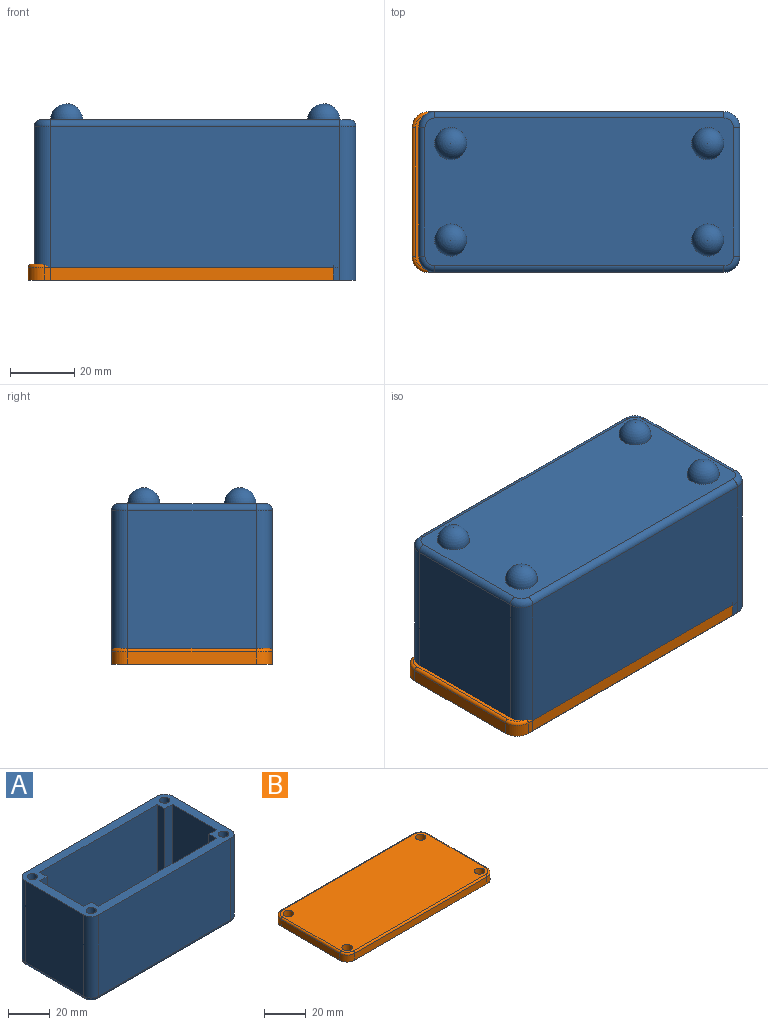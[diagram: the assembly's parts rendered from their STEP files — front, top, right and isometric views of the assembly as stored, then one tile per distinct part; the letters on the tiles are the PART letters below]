
ASSEMBLY  parts=2 mates=1
PART A: 43 faces, bbox 100.8x50.8x55 mm
  f0: plane 90x40mm, normal (0,0,1), area 3500mm2, adj f1,f2,f3,f4,f11,f12,f13,f14
  f1: plane 45x30mm, normal (-1,0,0), area 1350mm2, adj f0,f5,f16,f18
  f2: plane 45x30mm, normal (1,0,0), area 1350mm2, adj f0,f5,f12,f14
  f3: plane 80x45mm, normal (0,1,0), area 3600mm2, adj f0,f5,f13,f17
  f4: plane 80x45mm, normal (0,-1,0), area 3600mm2, adj f0,f5,f11,f15
  f5: plane 100x50mm, normal (0,0,1), area 1400mm2, adj f1,f2,f3,f4,f6,f7,f8,f9
  f6: plane 90x48mm, normal (0,1,0), area 4320mm2, adj f5,f27,f30,f39
  f7: plane 48x40mm, normal (-1,0,0), area 1920mm2, adj f5,f27,f28,f35
  f8: plane 90x48mm, normal (0,-1,0), area 4320mm2, adj f5,f28,f29,f38
  f9: plane 48x40mm, normal (1,0,0), area 1920mm2, adj f5,f29,f30,f42
  f10: plane 96x46mm, normal (0,0,-1), area 4094.1mm2, adj f31,f32,f33,f34,f35,f36,f37,f38
  f11: plane 45x5mm, normal (1,0,0), area 225mm2, adj f0,f4,f5,f12
  f12: plane 45x5mm, normal (0,-1,0), area 225mm2, adj f0,f2,f5,f11
  f13: plane 45x5mm, normal (1,0,0), area 225mm2, adj f0,f3,f5,f14
  f14: plane 45x5mm, normal (0,1,0), area 225mm2, adj f0,f2,f5,f13
  f15: plane 45x5mm, normal (-1,0,0), area 225mm2, adj f0,f4,f5,f16
  f16: plane 45x5mm, normal (0,-1,0), area 225mm2, adj f0,f1,f5,f15
  f17: plane 45x5mm, normal (-1,0,0), area 225mm2, adj f0,f3,f5,f18
  f18: plane 45x5mm, normal (0,1,0), area 225mm2, adj f0,f1,f5,f17
  f19: cylinder r=2.5mm len=12mm, axis (0,0,1), area 188.5mm2, adj f5,f20
  f20: cone r=0mm half-angle=59deg, axis (0,0,1), area 22.9mm2, adj f19
  f21: cylinder r=2.5mm len=12mm, axis (0,0,1), area 188.5mm2, adj f5,f22
  f22: cone r=0mm half-angle=59deg, axis (0,0,1), area 22.9mm2, adj f21
  f23: cylinder r=2.5mm len=12mm, axis (0,0,1), area 188.5mm2, adj f5,f24
  f24: cone r=0mm half-angle=59deg, axis (0,0,1), area 22.9mm2, adj f23
  f25: cylinder r=2.5mm len=12mm, axis (0,0,1), area 188.5mm2, adj f5,f26
  f26: cone r=0mm half-angle=59deg, axis (0,0,1), area 22.9mm2, adj f25
  f27: cylinder r=5mm len=48mm, axis (0,0,-1), area 377mm2, adj f5,f6,f7,f37
  f28: cylinder r=5mm len=48mm, axis (0,0,1), area 377mm2, adj f5,f7,f8,f36
  f29: cylinder r=5mm len=48mm, axis (0,0,-1), area 377mm2, adj f5,f8,f9,f40
  f30: cylinder r=5mm len=48mm, axis (0,0,1), area 377mm2, adj f5,f6,f9,f41
  f31: sphere r=5mm, area 157.1mm2, adj f10
  f32: sphere r=5mm, area 157.1mm2, adj f10
  f33: sphere r=5mm, area 157.1mm2, adj f10
  f34: sphere r=5mm, area 157.1mm2, adj f10
  f35: cylinder r=2mm len=40mm, axis (0,-1,0), area 125.7mm2, adj f7,f10,f36,f37
  f36: torus R=3mm, axis (0,0,1), area 21.1mm2, adj f10,f28,f35,f38
  f37: torus R=3mm, axis (0,0,1), area 21.1mm2, adj f10,f27,f35,f39
  f38: cylinder r=2mm len=90mm, axis (1,0,0), area 282.7mm2, adj f8,f10,f36,f40
  f39: cylinder r=2mm len=90mm, axis (-1,0,0), area 282.7mm2, adj f6,f10,f37,f41
  f40: torus R=3mm, axis (0,0,1), area 21.1mm2, adj f10,f29,f38,f42
  f41: torus R=3mm, axis (0,0,1), area 21.1mm2, adj f10,f30,f39,f42
  f42: cylinder r=2mm len=40mm, axis (0,1,0), area 125.7mm2, adj f9,f10,f40,f41
PART B: 22 faces, bbox 100.8x50.8x5 mm
  f0: plane 90x4mm, normal (0,1,0), area 360mm2, adj f1,f11,f13,f14
  f1: cylinder r=5mm len=5mm, axis (0,0,-1), area 31.4mm2, adj f0,f2,f13,f15
  f2: plane 40x4mm, normal (-1,0,0), area 160mm2, adj f1,f3,f13,f17
  f3: cylinder r=5mm len=5mm, axis (0,0,-1), area 31.4mm2, adj f2,f4,f13,f19
  f4: plane 90x4mm, normal (0,-1,0), area 360mm2, adj f3,f5,f13,f21
  f5: cylinder r=5mm len=5mm, axis (0,0,-1), area 31.4mm2, adj f4,f6,f13,f20
  f6: plane 40x4mm, normal (1,0,0), area 160mm2, adj f5,f11,f13,f18
  f7: cylinder r=2.52mm len=5.05mm, axis (0,0,-1), area 79.2mm2, adj f12,f13
  f8: cylinder r=2.58mm len=5.15mm, axis (0,0,-1), area 81mm2, adj f12,f13
  f9: cylinder r=2.56mm len=5.12mm, axis (0,0,-1), area 80.4mm2, adj f12,f13
  f10: cylinder r=2.49mm len=5mm, axis (0,0,-1), area 78.3mm2, adj f12,f13
  f11: cylinder r=5mm len=5mm, axis (0,0,-1), area 31.4mm2, adj f0,f6,f13,f16
  f12: plane 98x48mm, normal (0,0,1), area 4609.3mm2, adj f7,f8,f9,f10,f14,f15,f16,f17
  f13: plane 100x50mm, normal (0,0,-1), area 4897.6mm2, adj f0,f1,f2,f3,f4,f5,f6,f7
  f14: cylinder r=1mm len=90mm, axis (1,0,0), area 141.4mm2, adj f0,f12,f15,f16
  f15: torus R=4mm, axis (0,0,1), area 11.4mm2, adj f1,f12,f14,f17
  f16: torus R=4mm, axis (0,0,1), area 11.4mm2, adj f11,f12,f14,f18
  f17: cylinder r=1mm len=40mm, axis (0,1,0), area 62.8mm2, adj f2,f12,f15,f19
  f18: cylinder r=1mm len=40mm, axis (0,-1,0), area 62.8mm2, adj f6,f12,f16,f20
  f19: torus R=4mm, axis (0,0,1), area 11.4mm2, adj f3,f12,f17,f21
  f20: torus R=4mm, axis (0,0,1), area 11.4mm2, adj f5,f12,f18,f21
  f21: cylinder r=1mm len=90mm, axis (-1,0,0), area 141.4mm2, adj f4,f12,f19,f20
PLACE A rot(axis=(1,0,0),180deg) t=(71.38,-17.02,58.09)mm
PLACE B t=(69.38,-67.02,-41.91)mm
MATE slider A.f25 <-> B.f13  axis (0,0,-1) through (166.38,-62.02,8.09)mm
